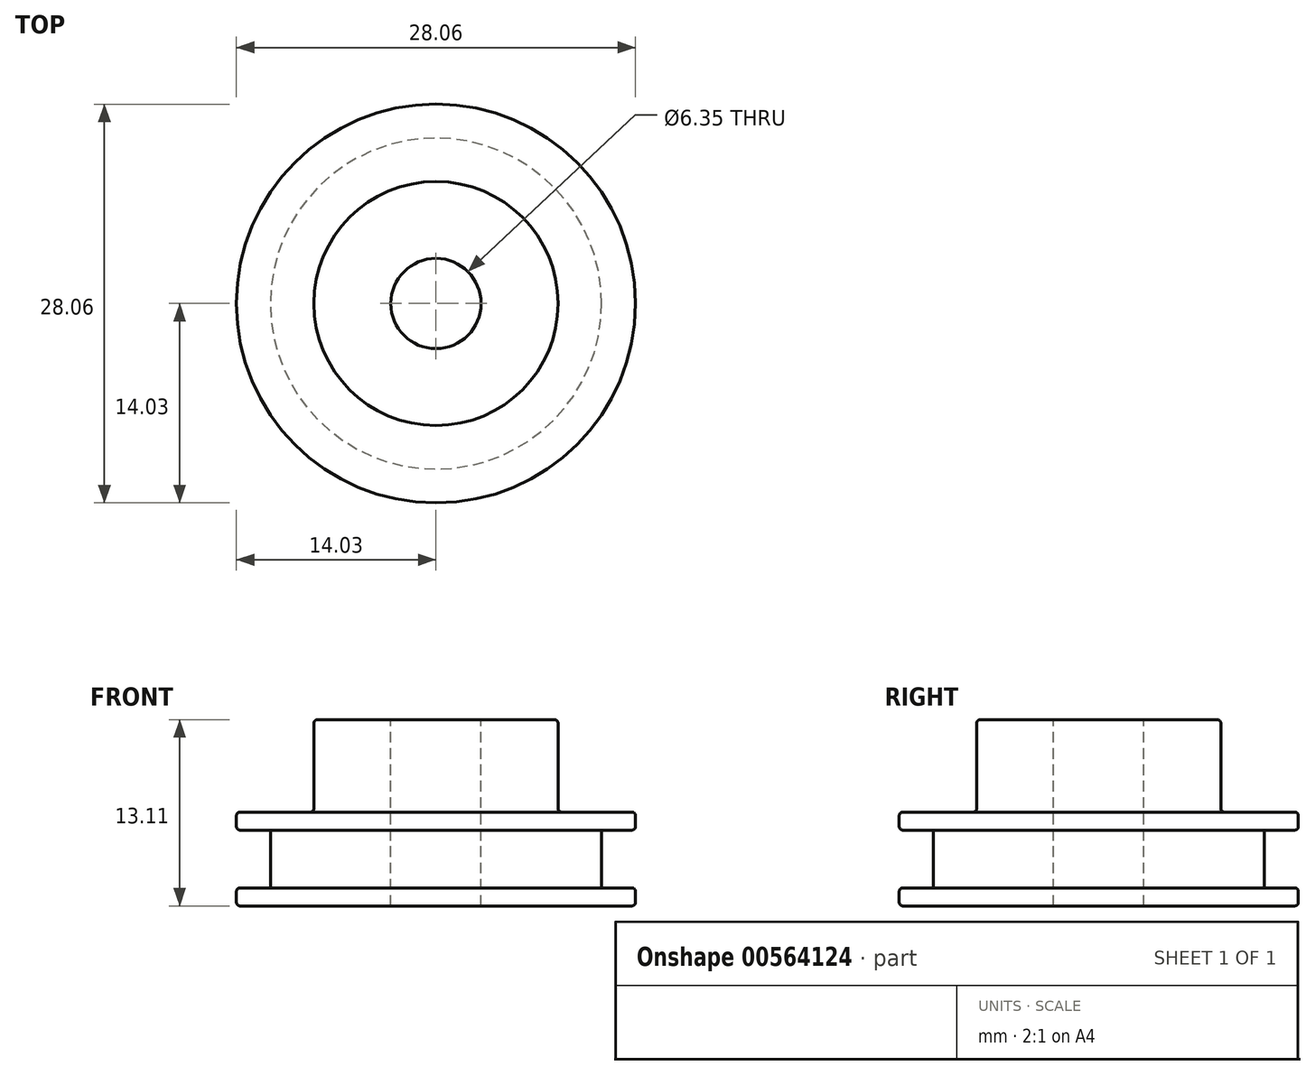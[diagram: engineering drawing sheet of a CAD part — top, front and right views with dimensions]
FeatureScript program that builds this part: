
annotation { "Feature Type Name" : "Feature", "Feature Type Description" : "" }
export const myFeature = defineFeature(function(context is Context, id is Id, definition is map)
    precondition{}
    {
        {
            var Q0;
            Q0=qCreatedBy(makeId("Front.planeOp"),FACE);
            var sketch = newSketch(context, id + "F0", { "sketchPlane" : qUnion([Q0])});
            skLineSegment(sketch, "E0", {"start": v(0, 2.3) * mm, "end": v(0, -3.8) * mm});
            skLineSegment(sketch, "E1", {"start": v(3.18, 0) * mm, "end": v(3.18, 13.1) * mm});
            skLineSegment(sketch, "E2", {"start": v(3.17, 13.1) * mm, "end": v(8.59, 13.1) * mm});
            skLineSegment(sketch, "E3", {"start": v(8.59, 13.1) * mm, "end": v(8.59, 6.6) * mm});
            skLineSegment(sketch, "E4", {"start": v(8.59, 6.6) * mm, "end": v(14.03, 6.6) * mm});
            skLineSegment(sketch, "E5", {"start": v(14.03, 6.6) * mm, "end": v(14.03, 5.33) * mm});
            skLineSegment(sketch, "E6", {"start": v(14.03, 5.33) * mm, "end": v(11.65, 5.33) * mm});
            skLineSegment(sketch, "E7", {"start": v(11.65, 5.33) * mm, "end": v(11.65, 1.27) * mm});
            skLineSegment(sketch, "E8", {"start": v(11.65, 1.27) * mm, "end": v(14.03, 1.27) * mm});
            skLineSegment(sketch, "E9", {"start": v(14.03, 1.27) * mm, "end": v(14.03, 0) * mm});
            skLineSegment(sketch, "E10", {"start": v(14.03, 0) * mm, "end": v(3.18, 0) * mm});
            skSolve(sketch);
        }
        {
            var Q0;
            Q0 = qSketchRegion(id + "F0", true);
            var Q1;
            Q1=sQuery(id+"F0.wireOp",EDGE,"E0");
            revolve(context, id + "F1", {"entities" : qUnion([Q0]), "axis" : qUnion([Q1]), "revolveType" : RevolveType.FULL});
        }
        {
            var Q0;
            Q0=makeQuery(id+"F1.opRevolve","SWEPT_EDGE",EDGE,{"disambiguationData":[OSD([sQuery(id+"F0.wireOp",EDGE,"E2"),sQuery(id+"F0.wireOp",EDGE,"E3")])]});
            var Q1;
            Q1=makeQuery(id+"F1.opRevolve","SWEPT_FACE",FACE,{"disambiguationData":[OSD([sQuery(id+"F0.wireOp",EDGE,"E5")])]});
            var Q2;
            Q2=makeQuery(id+"F1.opRevolve","SWEPT_FACE",FACE,{"disambiguationData":[OSD([sQuery(id+"F0.wireOp",EDGE,"E9")])]});
            var Q3;
            Q3=makeQuery(id+"F1.opRevolve","SWEPT_EDGE",EDGE,{"disambiguationData":[OSD([sQuery(id+"F0.wireOp",EDGE,"E3"),sQuery(id+"F0.wireOp",EDGE,"E4")])]});
            fillet(context, id + "F2", {"entities" : qUnion([Q0, Q1, Q2, Q3]), "radius" : 0.25 * mm, "tangentPropagation" : true, "allowEdgeOverflow" : false});
        }
    });
